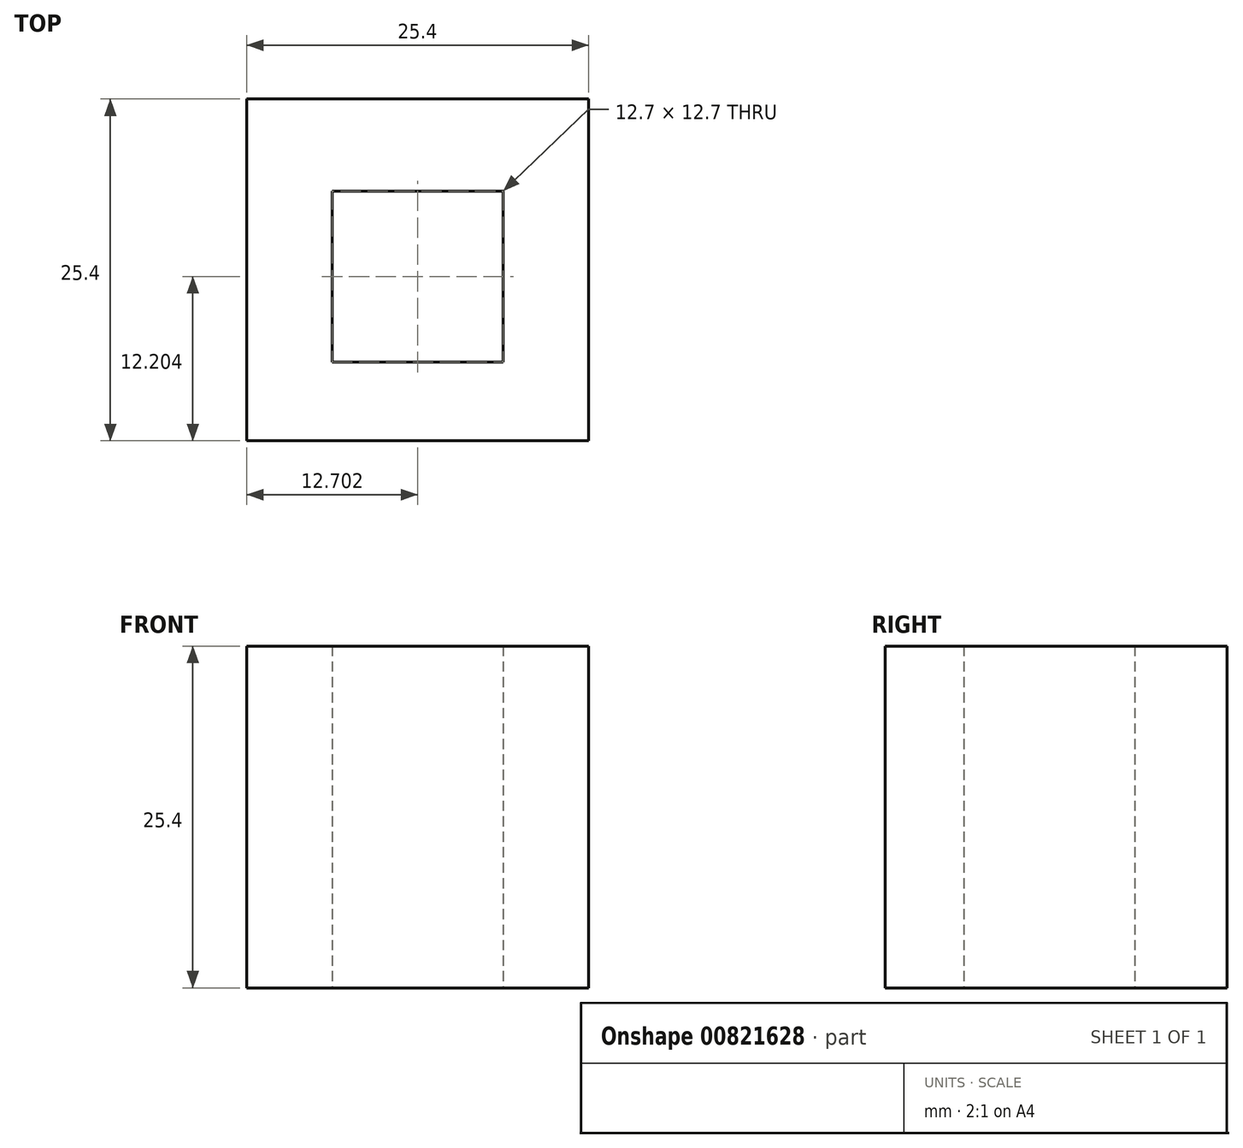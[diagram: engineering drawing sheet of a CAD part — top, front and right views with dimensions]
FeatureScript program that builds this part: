
annotation { "Feature Type Name" : "Feature", "Feature Type Description" : "" }
export const myFeature = defineFeature(function(context is Context, id is Id, definition is map)
    precondition{}
    {
        {
            var Q0;
            Q0=qCreatedBy(makeId("Top.planeOp"),FACE);
            var sketch = newSketch(context, id + "F0", { "sketchPlane" : qUnion([Q0])});
            skLineSegment(sketch, "E0.bottom", {"start": v(-13.37, 7.42) * mm, "end": v(12.03, 7.42) * mm});
            skLineSegment(sketch, "E0.top", {"start": v(-13.37, -17.98) * mm, "end": v(12.03, -17.98) * mm});
            skLineSegment(sketch, "E0.left", {"start": v(-13.37, 7.42) * mm, "end": v(-13.37, -17.98) * mm});
            skLineSegment(sketch, "E0.right", {"start": v(12.03, 7.42) * mm, "end": v(12.03, -17.98) * mm});
            skLineSegment(sketch, "E1.bottom", {"start": v(-7.02, 0.57) * mm, "end": v(5.68, 0.57) * mm});
            skLineSegment(sketch, "E1.top", {"start": v(-7.02, -12.13) * mm, "end": v(5.68, -12.13) * mm});
            skLineSegment(sketch, "E1.left", {"start": v(-7.02, 0.57) * mm, "end": v(-7.02, -12.13) * mm});
            skLineSegment(sketch, "E1.right", {"start": v(5.68, 0.57) * mm, "end": v(5.68, -12.13) * mm});
            skSolve(sketch);
        }
        {
            var Q0;
            Q0=makeQuery(id+"F0.imprint","IMPRINT",FACE,{"disambiguationData":[TD([[makeQuery(id+"F0.imprint","IMPRINT",EDGE,{"derivedFrom":sQuery(id+"F0.wireOp",EDGE,"E0.bottom")}),-1.0]])]});
            extrude(context, id + "F1", {"entities" : qUnion([Q0]), "depth" : 25.4 * mm, "offsetDistance" : 25.4 * mm});
        }
    });
